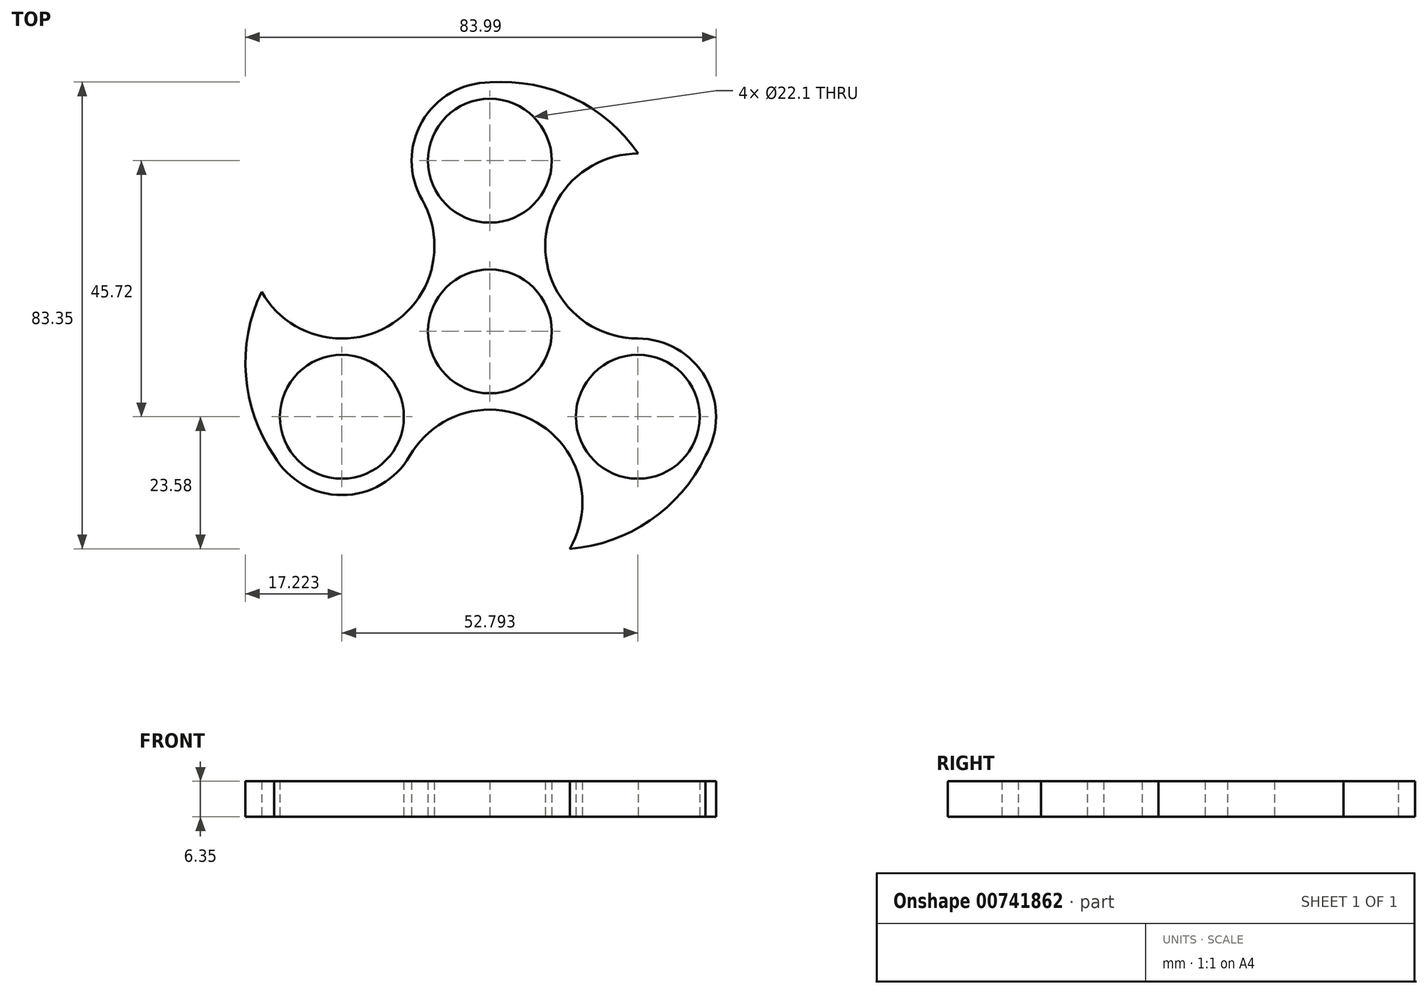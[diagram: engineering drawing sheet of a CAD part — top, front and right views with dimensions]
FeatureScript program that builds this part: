
annotation { "Feature Type Name" : "Feature", "Feature Type Description" : "" }
export const myFeature = defineFeature(function(context is Context, id is Id, definition is map)
    precondition{}
    {
        {
            var Q0;
            Q0=qCreatedBy(makeId("Top.planeOp"),FACE);
            var sketch = newSketch(context, id + "F0", { "sketchPlane" : qUnion([Q0])});
            skCircle(sketch, "E0", {"center": v(0, 0) * mm, "radius": 13.97 * mm});
            skCircle(sketch, "E1", {"center": v(0, 0) * mm, "radius": 11.05 * mm});
            skLineSegment(sketch, "E2", {"start": v(0, 0) * mm, "end": v(0, 30.48) * mm});
            skCircle(sketch, "E3", {"center": v(0, 30.48) * mm, "radius": 11.05 * mm});
            skCircle(sketch, "E4", {"center": v(0, 30.48) * mm, "radius": 13.97 * mm});
            skLineSegment(sketch, "E5.1.0", {"start": v(0, 0) * mm, "end": v(-26.4, -15.24) * mm});
            skCircle(sketch, "E5.1.1", {"center": v(-26.4, -15.24) * mm, "radius": 13.97 * mm});
            skLineSegment(sketch, "E5.2.0", {"start": v(0, 0) * mm, "end": v(26.4, -15.24) * mm});
            skCircle(sketch, "E5.2.1", {"center": v(26.4, -15.24) * mm, "radius": 13.97 * mm});
            skCircle(sketch, "E6.1.1", {"center": v(-26.4, -15.24) * mm, "radius": 11.05 * mm});
            skCircle(sketch, "E6.2.1", {"center": v(26.4, -15.24) * mm, "radius": 11.05 * mm});
            skLineSegment(sketch, "E7", {"start": v(0, 0) * mm, "end": v(0, -30.48) * mm});
            skArc(sketch, "E8", {"start": v(14.25, -38.82) * mm, "mid": v(8.3, -16.2) * mm, "end": v(-14.3, -22.22) * mm});
            skArc(sketch, "E9.1.1", {"start": v(26.49, 31.75) * mm, "mid": v(9.89, 15.29) * mm, "end": v(26.4, -1.27) * mm});
            skArc(sketch, "E9.2.1", {"start": v(-40.74, 7.07) * mm, "mid": v(-18.18, 0.92) * mm, "end": v(-12.1, 23.5) * mm});
            skPoint(sketch, "E10", {"position": v(0, 44.45) * mm});
            skArc(sketch, "E11", {"start": v(26.49, 31.75) * mm, "mid": v(14.94, 41.64) * mm, "end": v(0, 44.45) * mm});
            skArc(sketch, "E12.1.1", {"start": v(-40.74, 7.07) * mm, "mid": v(-43.53, -7.88) * mm, "end": v(-38.5, -22.22) * mm});
            skArc(sketch, "E12.2.1", {"start": v(14.25, -38.82) * mm, "mid": v(28.6, -33.76) * mm, "end": v(38.5, -22.23) * mm});
            skSolve(sketch);
        }
        {
            var Q0;
            Q0 = qSketchRegion(id + "F0", true);
            extrude(context, id + "F1", {"entities" : qUnion([Q0]), "depth" : 6.35 * mm, "offsetDistance" : 25.4 * mm});
        }
    });
